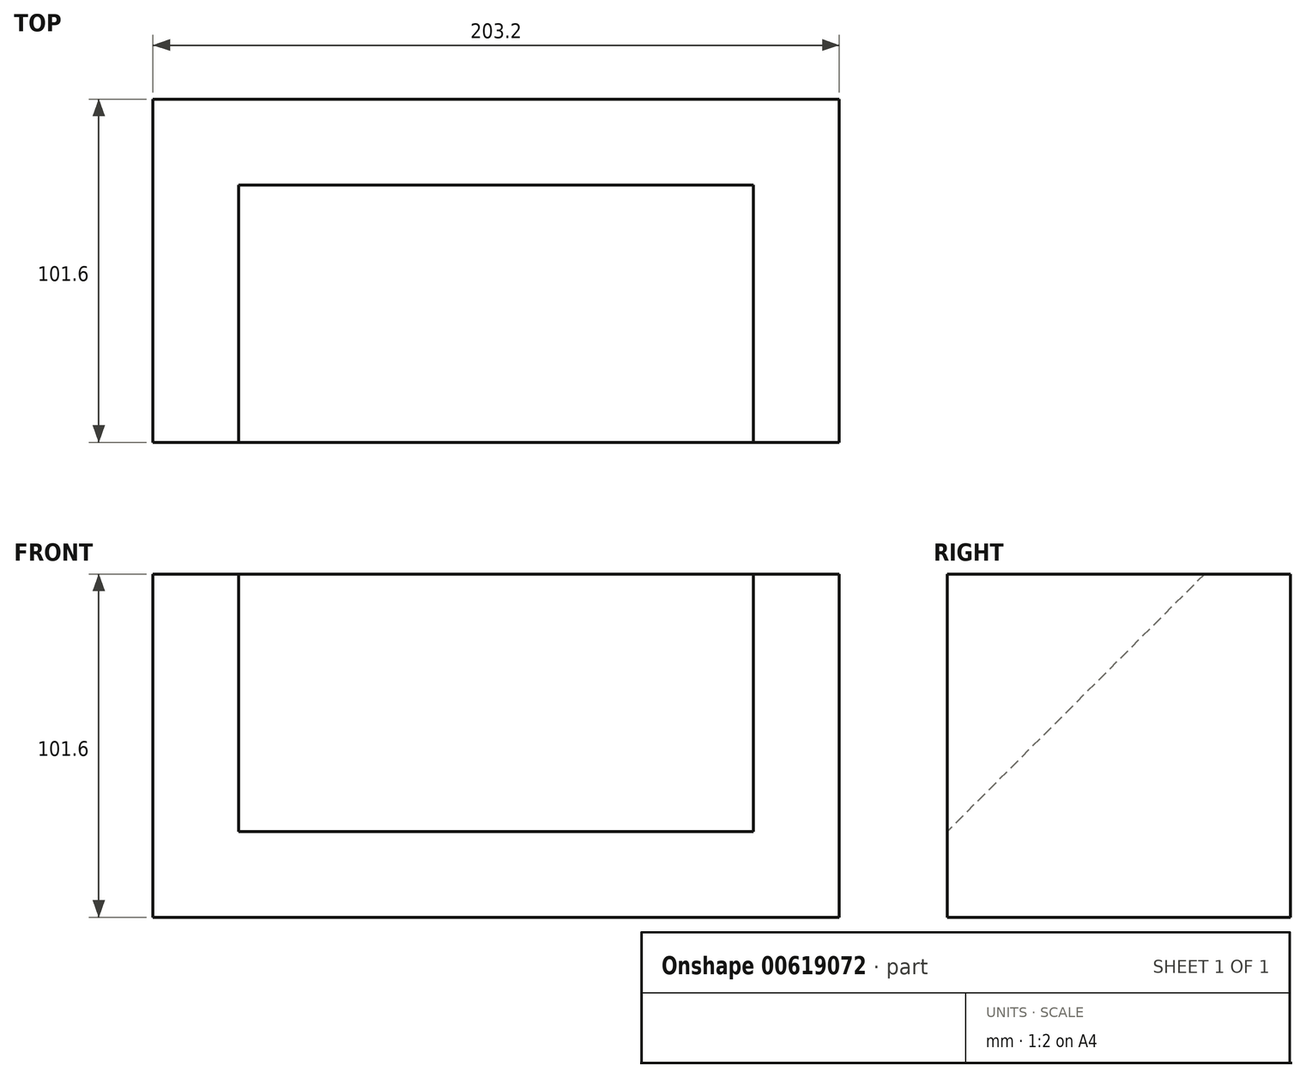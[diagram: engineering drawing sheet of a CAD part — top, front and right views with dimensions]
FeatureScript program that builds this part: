
annotation { "Feature Type Name" : "Feature", "Feature Type Description" : "" }
export const myFeature = defineFeature(function(context is Context, id is Id, definition is map)
    precondition{}
    {
        {
            var Q0;
            Q0=qCreatedBy(makeId("Right.planeOp"),FACE);
            var sketch = newSketch(context, id + "F0", { "sketchPlane" : qUnion([Q0])});
            skLineSegment(sketch, "E0.bottom", {"start": v(-48.6, -28.1) * mm, "end": v(53, -28.1) * mm});
            skLineSegment(sketch, "E0.top", {"start": v(27.6, 73.5) * mm, "end": v(53, 73.5) * mm});
            skLineSegment(sketch, "E0.left", {"start": v(-48.6, -28.1) * mm, "end": v(-48.6, -2.7) * mm});
            skLineSegment(sketch, "E0.right", {"start": v(53, -28.1) * mm, "end": v(53, 73.5) * mm});
            skLineSegment(sketch, "E1", {"start": v(27.6, 73.5) * mm, "end": v(-48.6, -2.7) * mm});
            skSolve(sketch);
        }
        {
            var Q0;
            Q0 = qSketchRegion(id + "F0", true);
            extrude(context, id + "F1", {"entities" : qUnion([Q0]), "depth" : 203.2 * mm, "offsetDistance" : 25.4 * mm});
        }
        {
            var Q0;
            Q0=makeQuery(id+"F1.opExtrude","SWEPT_FACE",FACE,{"disambiguationData":[OSD([sQuery(id+"F0.wireOp",EDGE,"E0.right")])]});
            var sketch = newSketch(context, id + "F2", { "sketchPlane" : qUnion([Q0])});
            skLineSegment(sketch, "E2.bottom", {"start": v(0, 73.5) * mm, "end": v(-25.4, 73.5) * mm});
            skLineSegment(sketch, "E2.top", {"start": v(0, -28.1) * mm, "end": v(-25.4, -28.1) * mm});
            skLineSegment(sketch, "E2.left", {"start": v(0, 73.5) * mm, "end": v(0, -28.1) * mm});
            skLineSegment(sketch, "E2.right", {"start": v(-25.4, 73.5) * mm, "end": v(-25.4, -28.1) * mm});
            skLineSegment(sketch, "E3.bottom", {"start": v(-203.2, 73.5) * mm, "end": v(-177.8, 73.5) * mm});
            skLineSegment(sketch, "E3.top", {"start": v(-203.2, -28.1) * mm, "end": v(-177.8, -28.1) * mm});
            skLineSegment(sketch, "E3.left", {"start": v(-203.2, 73.5) * mm, "end": v(-203.2, -28.1) * mm});
            skLineSegment(sketch, "E3.right", {"start": v(-177.8, 73.5) * mm, "end": v(-177.8, -28.1) * mm});
            skSolve(sketch);
        }
        {
            var Q0;
            Q0 = qSketchRegion(id + "F2", true);
            extrude(context, id + "F3", {"entities" : qUnion([Q0]), "operationType" : NewBodyOperationType.ADD, "depth" : 0 * mm, "offsetDistance" : 25.4 * mm, "hasSecondDirection" : true, "secondDirectionOppositeDirection" : true, "secondDirectionDepth" : 101.6 * mm});
        }
    });
